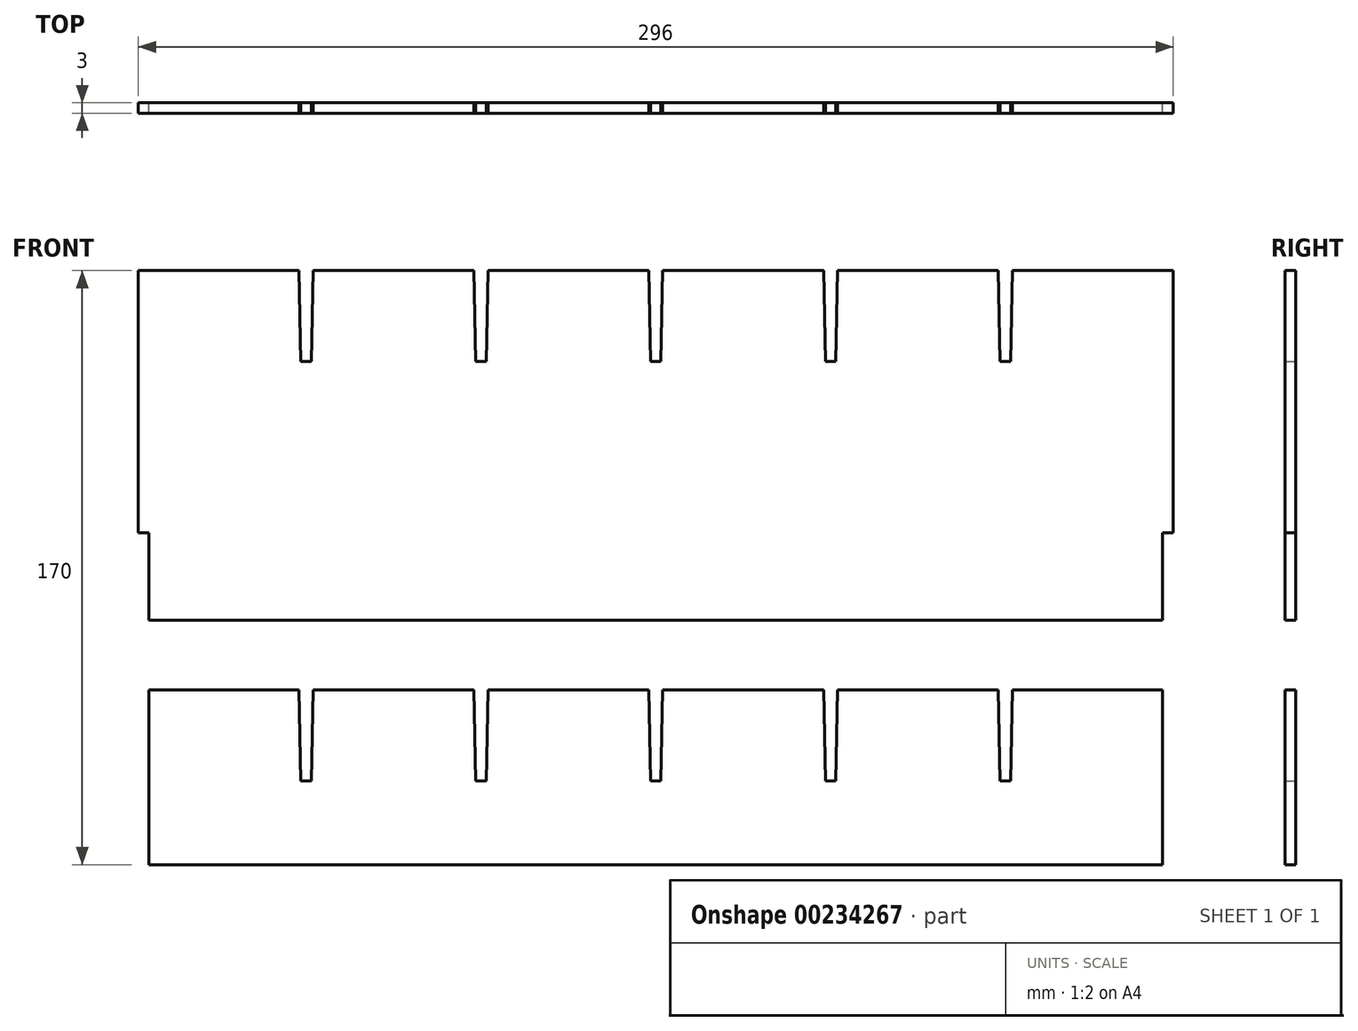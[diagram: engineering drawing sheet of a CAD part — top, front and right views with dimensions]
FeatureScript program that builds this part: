
annotation { "Feature Type Name" : "Feature", "Feature Type Description" : "" }
export const myFeature = defineFeature(function(context is Context, id is Id, definition is map)
    precondition{}
    {
        {
            var Q0;
            Q0=qCreatedBy(makeId("Front.planeOp"),FACE);
            var sketch = newSketch(context, id + "F0", { "sketchPlane" : qUnion([Q0])});
            skLineSegment(sketch, "E0.bottom", {"start": v(10, 10) * mm, "end": v(300, 10) * mm});
            skLineSegment(sketch, "E0.top", {"start": v(10, 110) * mm, "end": v(300, 110) * mm});
            skLineSegment(sketch, "E0.left", {"start": v(10, 10) * mm, "end": v(10, 110) * mm});
            skLineSegment(sketch, "E0.right", {"start": v(300, 10) * mm, "end": v(300, 110) * mm});
            skLineSegment(sketch, "E1", {"start": v(10, 84) * mm, "end": v(300, 84) * mm, "construction": true});
            skLineSegment(sketch, "E2", {"start": v(53, 110) * mm, "end": v(53.5, 84) * mm});
            skLineSegment(sketch, "E3", {"start": v(56.5, 84) * mm, "end": v(57, 110) * mm});
            skLineSegment(sketch, "E4", {"start": v(53, 110) * mm, "end": v(57, 110) * mm});
            skLineSegment(sketch, "E5", {"start": v(53.5, 84) * mm, "end": v(56.5, 84) * mm});
            skPoint(sketch, "E6", {"position": v(55, 110) * mm});
            skPoint(sketch, "E7", {"position": v(55, 84) * mm});
            skPoint(sketch, "E8.1.0.0", {"position": v(105, 110) * mm});
            skLineSegment(sketch, "E8.1.0.1", {"start": v(103, 110) * mm, "end": v(103.5, 84) * mm});
            skLineSegment(sketch, "E8.1.0.2", {"start": v(106.5, 84) * mm, "end": v(107, 110) * mm});
            skPoint(sketch, "E8.1.0.3", {"position": v(105, 84) * mm});
            skLineSegment(sketch, "E8.1.0.4", {"start": v(103, 110) * mm, "end": v(107, 110) * mm});
            skLineSegment(sketch, "E8.1.0.5", {"start": v(103.5, 84) * mm, "end": v(106.5, 84) * mm});
            skPoint(sketch, "E8.2.0.0", {"position": v(155, 110) * mm});
            skLineSegment(sketch, "E8.2.0.1", {"start": v(153, 110) * mm, "end": v(153.5, 84) * mm});
            skLineSegment(sketch, "E8.2.0.2", {"start": v(156.5, 84) * mm, "end": v(157, 110) * mm});
            skPoint(sketch, "E8.2.0.3", {"position": v(155, 84) * mm});
            skLineSegment(sketch, "E8.2.0.4", {"start": v(153, 110) * mm, "end": v(157, 110) * mm});
            skLineSegment(sketch, "E8.2.0.5", {"start": v(153.5, 84) * mm, "end": v(156.5, 84) * mm});
            skPoint(sketch, "E8.3.0.0", {"position": v(205, 110) * mm});
            skLineSegment(sketch, "E8.3.0.1", {"start": v(203, 110) * mm, "end": v(203.5, 84) * mm});
            skLineSegment(sketch, "E8.3.0.2", {"start": v(206.5, 84) * mm, "end": v(207, 110) * mm});
            skPoint(sketch, "E8.3.0.3", {"position": v(205, 84) * mm});
            skLineSegment(sketch, "E8.3.0.4", {"start": v(203, 110) * mm, "end": v(207, 110) * mm});
            skLineSegment(sketch, "E8.3.0.5", {"start": v(203.5, 84) * mm, "end": v(206.5, 84) * mm});
            skPoint(sketch, "E8.4.0.0", {"position": v(255, 110) * mm});
            skLineSegment(sketch, "E8.4.0.1", {"start": v(253, 110) * mm, "end": v(253.5, 84) * mm});
            skLineSegment(sketch, "E8.4.0.2", {"start": v(256.5, 84) * mm, "end": v(257, 110) * mm});
            skPoint(sketch, "E8.4.0.3", {"position": v(255, 84) * mm});
            skLineSegment(sketch, "E8.4.0.4", {"start": v(253, 110) * mm, "end": v(257, 110) * mm});
            skLineSegment(sketch, "E8.4.0.5", {"start": v(253.5, 84) * mm, "end": v(256.5, 84) * mm});
            skLineSegment(sketch, "E8.direction1", {"start": v(53.5, 84) * mm, "end": v(103.5, 84) * mm, "construction": true});
            skPoint(sketch, "E9.oppositeSnap0", {"position": v(10, 60) * mm});
            skLineSegment(sketch, "E9.bottom", {"start": v(10, 110) * mm, "end": v(7, 110) * mm});
            skLineSegment(sketch, "E9.top", {"start": v(10, 60) * mm, "end": v(7, 60) * mm});
            skLineSegment(sketch, "E9.left", {"start": v(10, 110) * mm, "end": v(10, 60) * mm});
            skLineSegment(sketch, "E9.right", {"start": v(7, 110) * mm, "end": v(7, 60) * mm});
            skPoint(sketch, "E10.oppositeSnap0", {"position": v(300, 60) * mm});
            skLineSegment(sketch, "E10.bottom", {"start": v(300, 110) * mm, "end": v(303, 110) * mm});
            skLineSegment(sketch, "E10.top", {"start": v(300, 60) * mm, "end": v(303, 60) * mm});
            skLineSegment(sketch, "E10.left", {"start": v(300, 110) * mm, "end": v(300, 60) * mm});
            skLineSegment(sketch, "E10.right", {"start": v(303, 110) * mm, "end": v(303, 60) * mm});
            skLineSegment(sketch, "E11.top", {"start": v(10, 35) * mm, "end": v(7, 35) * mm});
            skLineSegment(sketch, "E11.left", {"start": v(10, 60) * mm, "end": v(10, 35) * mm});
            skLineSegment(sketch, "E11.right", {"start": v(7, 60) * mm, "end": v(7, 35) * mm});
            skLineSegment(sketch, "E12.top", {"start": v(300, 35) * mm, "end": v(303, 35) * mm});
            skLineSegment(sketch, "E12.left", {"start": v(300, 60) * mm, "end": v(300, 35) * mm});
            skLineSegment(sketch, "E12.right", {"start": v(303, 60) * mm, "end": v(303, 35) * mm});
            skSolve(sketch);
        }
        {
            var Q0;
            Q0=makeQuery(id+"F0.imprint","IMPRINT",FACE,{"disambiguationData":[TD([[makeQuery(id+"F0.imprint","IMPRINT",EDGE,{"derivedFrom":sQuery(id+"F0.wireOp",EDGE,"E0.bottom")}),1.0]])]});
            var Q1;
            Q1=makeQuery(id+"F0.imprint","IMPRINT",FACE,{"disambiguationData":[TD([[makeQuery(id+"F0.imprint","IMPRINT",EDGE,{"derivedFrom":sQuery(id+"F0.wireOp",EDGE,"E9.bottom")}),1.0]])]});
            var Q2;
            Q2=makeQuery(id+"F0.imprint","IMPRINT",FACE,{"disambiguationData":[TD([[makeQuery(id+"F0.imprint","IMPRINT",EDGE,{"derivedFrom":sQuery(id+"F0.wireOp",EDGE,"E10.bottom")}),-1.0]])]});
            var Q3;
            Q3=makeQuery(id+"F0.imprint","IMPRINT",FACE,{"disambiguationData":[TD([[makeQuery(id+"F0.imprint","IMPRINT",EDGE,{"derivedFrom":sQuery(id+"F0.wireOp",EDGE,"E9.top")}),1.0]])]});
            var Q4;
            Q4=makeQuery(id+"F0.imprint","IMPRINT",FACE,{"disambiguationData":[TD([[makeQuery(id+"F0.imprint","IMPRINT",EDGE,{"derivedFrom":sQuery(id+"F0.wireOp",EDGE,"E10.top")}),-1.0]])]});
            extrude(context, id + "F1", {"entities" : qUnion([Q0, Q1, Q2, Q3, Q4]), "depth" : 3 * mm});
        }
        {
            var Q0;
            Q0=qCreatedBy(makeId("Front.planeOp"),FACE);
            var sketch = newSketch(context, id + "F2", { "sketchPlane" : qUnion([Q0])});
            skLineSegment(sketch, "E13.bottom", {"start": v(10, -60) * mm, "end": v(300, -60) * mm});
            skLineSegment(sketch, "E13.top", {"start": v(10, -10) * mm, "end": v(300, -10) * mm});
            skLineSegment(sketch, "E13.left", {"start": v(10, -60) * mm, "end": v(10, -10) * mm});
            skLineSegment(sketch, "E13.right", {"start": v(300, -60) * mm, "end": v(300, -10) * mm});
            skLineSegment(sketch, "E14", {"start": v(10, -36) * mm, "end": v(300, -36) * mm, "construction": true});
            skLineSegment(sketch, "E15", {"start": v(53, -10) * mm, "end": v(53.5, -36) * mm});
            skLineSegment(sketch, "E16", {"start": v(56.5, -36) * mm, "end": v(57, -10) * mm});
            skLineSegment(sketch, "E17", {"start": v(53, -10) * mm, "end": v(57, -10) * mm});
            skLineSegment(sketch, "E18", {"start": v(53.5, -36) * mm, "end": v(56.5, -36) * mm});
            skPoint(sketch, "E19", {"position": v(55, -10) * mm});
            skPoint(sketch, "E20", {"position": v(55, -36) * mm});
            skPoint(sketch, "E21.1.0.0", {"position": v(105, -10) * mm});
            skLineSegment(sketch, "E21.1.0.1", {"start": v(103, -10) * mm, "end": v(103.5, -36) * mm});
            skLineSegment(sketch, "E21.1.0.2", {"start": v(106.5, -36) * mm, "end": v(107, -10) * mm});
            skPoint(sketch, "E21.1.0.3", {"position": v(105, -36) * mm});
            skLineSegment(sketch, "E21.1.0.4", {"start": v(103, -10) * mm, "end": v(107, -10) * mm});
            skLineSegment(sketch, "E21.1.0.5", {"start": v(103.5, -36) * mm, "end": v(106.5, -36) * mm});
            skPoint(sketch, "E21.2.0.0", {"position": v(155, -10) * mm});
            skLineSegment(sketch, "E21.2.0.1", {"start": v(153, -10) * mm, "end": v(153.5, -36) * mm});
            skLineSegment(sketch, "E21.2.0.2", {"start": v(156.5, -36) * mm, "end": v(157, -10) * mm});
            skPoint(sketch, "E21.2.0.3", {"position": v(155, -36) * mm});
            skLineSegment(sketch, "E21.2.0.4", {"start": v(153, -10) * mm, "end": v(157, -10) * mm});
            skLineSegment(sketch, "E21.2.0.5", {"start": v(153.5, -36) * mm, "end": v(156.5, -36) * mm});
            skPoint(sketch, "E21.3.0.0", {"position": v(205, -10) * mm});
            skLineSegment(sketch, "E21.3.0.1", {"start": v(203, -10) * mm, "end": v(203.5, -36) * mm});
            skLineSegment(sketch, "E21.3.0.2", {"start": v(206.5, -36) * mm, "end": v(207, -10) * mm});
            skPoint(sketch, "E21.3.0.3", {"position": v(205, -36) * mm});
            skLineSegment(sketch, "E21.3.0.4", {"start": v(203, -10) * mm, "end": v(207, -10) * mm});
            skLineSegment(sketch, "E21.3.0.5", {"start": v(203.5, -36) * mm, "end": v(206.5, -36) * mm});
            skPoint(sketch, "E21.4.0.0", {"position": v(255, -10) * mm});
            skLineSegment(sketch, "E21.4.0.1", {"start": v(253, -10) * mm, "end": v(253.5, -36) * mm});
            skLineSegment(sketch, "E21.4.0.2", {"start": v(256.5, -36) * mm, "end": v(257, -10) * mm});
            skPoint(sketch, "E21.4.0.3", {"position": v(255, -36) * mm});
            skLineSegment(sketch, "E21.4.0.4", {"start": v(253, -10) * mm, "end": v(257, -10) * mm});
            skLineSegment(sketch, "E21.4.0.5", {"start": v(253.5, -36) * mm, "end": v(256.5, -36) * mm});
            skLineSegment(sketch, "E21.direction1", {"start": v(53.5, -36) * mm, "end": v(103.5, -36) * mm, "construction": true});
            skSolve(sketch);
        }
        {
            var Q0;
            Q0=makeQuery(id+"F2.imprint","IMPRINT",FACE,{"disambiguationData":[TD([[makeQuery(id+"F2.imprint","IMPRINT",EDGE,{"derivedFrom":sQuery(id+"F2.wireOp",EDGE,"E13.bottom")}),1.0]])]});
            extrude(context, id + "F3", {"entities" : qUnion([Q0]), "depth" : 3 * mm});
        }
    });
